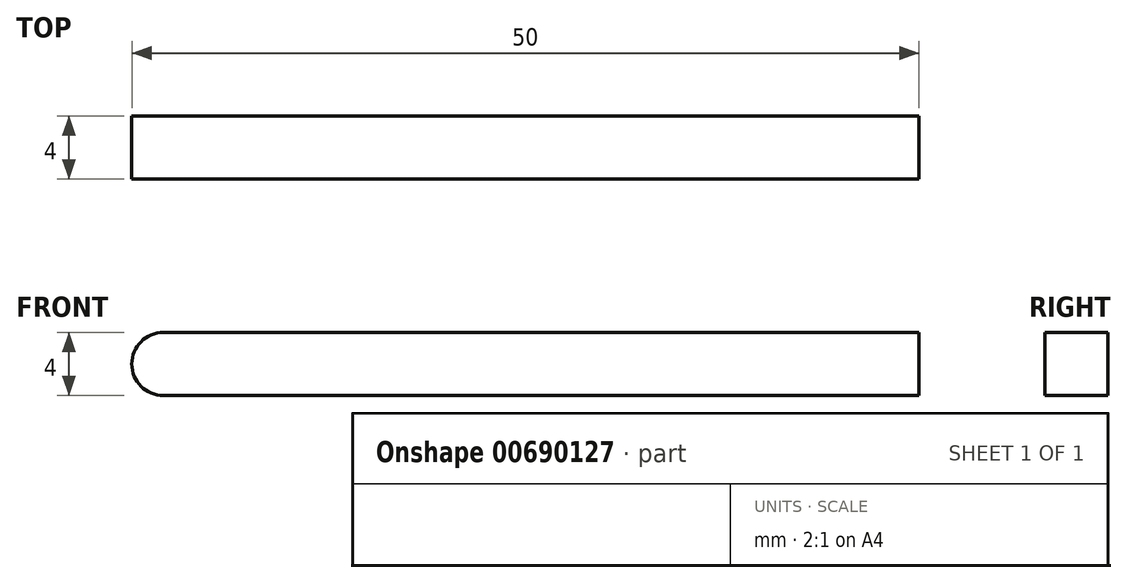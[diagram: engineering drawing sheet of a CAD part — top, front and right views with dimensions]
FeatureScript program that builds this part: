
annotation { "Feature Type Name" : "Feature", "Feature Type Description" : "" }
export const myFeature = defineFeature(function(context is Context, id is Id, definition is map)
    precondition{}
    {
        {
            var Q0;
            Q0=qCreatedBy(makeId("Top.planeOp"),FACE);
            var sketch = newSketch(context, id + "F0", { "sketchPlane" : qUnion([Q0])});
            skLineSegment(sketch, "E0.bottom", {"start": v(-2.02, 1.68) * mm, "end": v(47.98, 1.68) * mm});
            skLineSegment(sketch, "E0.top", {"start": v(-2.02, -2.32) * mm, "end": v(47.98, -2.32) * mm});
            skLineSegment(sketch, "E0.left", {"start": v(-2.02, 1.68) * mm, "end": v(-2.02, -2.32) * mm});
            skLineSegment(sketch, "E0.right", {"start": v(47.98, 1.68) * mm, "end": v(47.98, -2.32) * mm});
            skSolve(sketch);
        }
        {
            var Q0;
            Q0 = qSketchRegion(id + "F0", true);
            extrude(context, id + "F1", {"entities" : qUnion([Q0]), "depth" : 4 * mm, "offsetDistance" : 25 * mm});
        }
        {
            var Q0;
            Q0=makeQuery(id+"F1.opExtrude","CAP_EDGE",EDGE,{"disambiguationData":[OSD([sQuery(id+"F0.wireOp",EDGE,"E0.left")])],"isStart":true});
            var Q1;
            Q1=makeQuery(id+"F1.opExtrude","CAP_EDGE",EDGE,{"disambiguationData":[OSD([sQuery(id+"F0.wireOp",EDGE,"E0.left")])],"isStart":false});
            fillet(context, id + "F2", {"entities" : qUnion([Q0, Q1]), "radius" : 2 * mm, "tangentPropagation" : true, "allowEdgeOverflow" : false});
        }
    });
